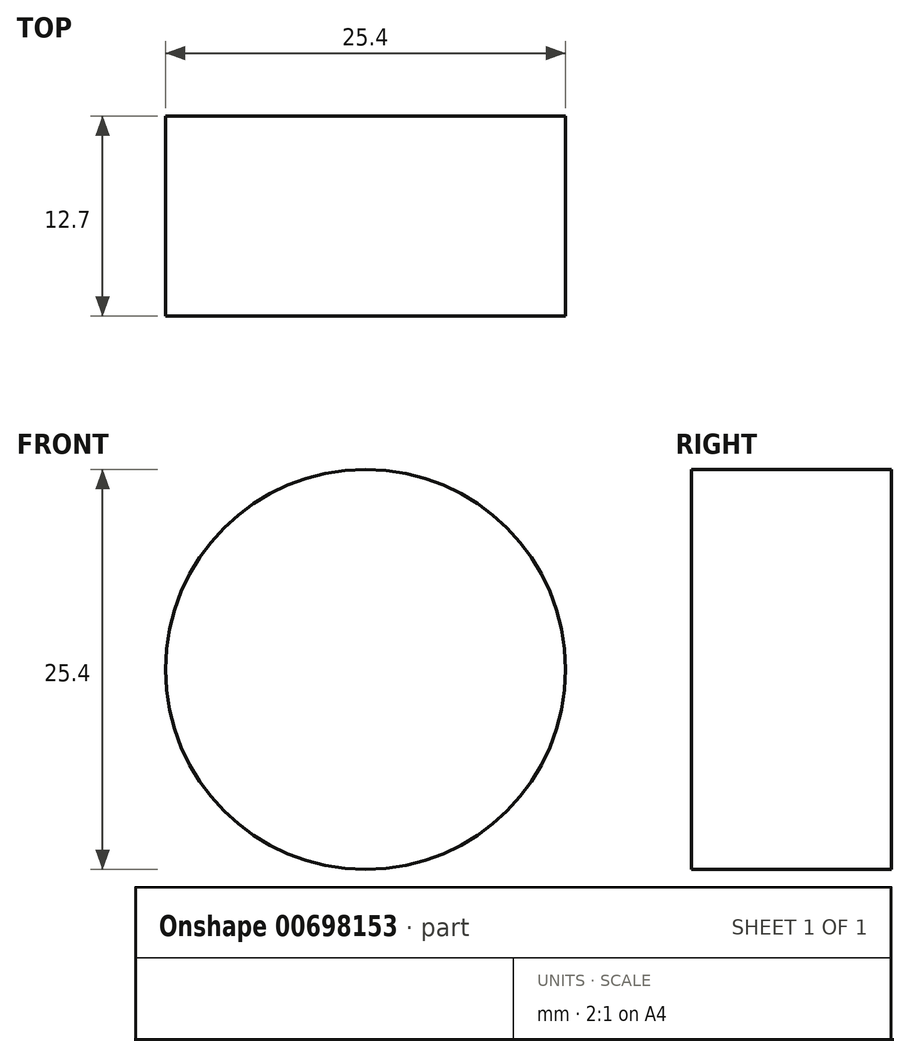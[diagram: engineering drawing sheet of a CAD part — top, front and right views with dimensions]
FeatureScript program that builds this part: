
annotation { "Feature Type Name" : "Feature", "Feature Type Description" : "" }
export const myFeature = defineFeature(function(context is Context, id is Id, definition is map)
    precondition{}
    {
        {
            var Q0;
            Q0=qCreatedBy(makeId("Front.planeOp"),FACE);
            var sketch = newSketch(context, id + "F0", { "sketchPlane" : qUnion([Q0])});
            skCircle(sketch, "E0", {"center": v(0, 0) * mm, "radius": 12.7 * mm});
            skSolve(sketch);
        }
        {
            var Q0;
            Q0=qSketchRegion(id+"F0",true);
            extrude(context, id + "F1", {"entities" : qUnion([Q0]), "depth" : 12.7 * mm, "offsetDistance" : 25.4 * mm});
        }
    });
